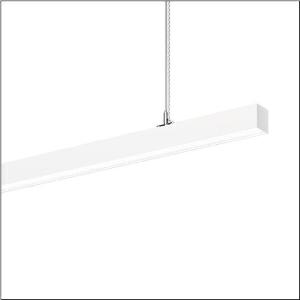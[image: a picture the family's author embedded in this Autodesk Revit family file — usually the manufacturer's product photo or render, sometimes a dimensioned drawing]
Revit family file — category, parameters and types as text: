
# Revit family: silica_r__21_51mx33tbt9w_4d61
name_source: partatom
category: Lighting Fixtures
units: mm (PartAtom-declared; Revit-internal decimal feet)

## family parameters
Cut with Voids When Loaded = No
Host = Face
Light Source = No
Part Type = Normal
Room Calculation Point = No
Round Connector Dimension = Use Diameter
Shared = No

## types (1)
- --- (1 x LED, 7170 lm, 67.4 W, 6500K)
    Apparent Load = 67 VA
    CIE Flux Codes = 78 96 99 56 100
    Color Rendering = 80
    Color Temperature = 6500K
    Default Elevation = 1800 mm
    Description = Silica® 21, office luminaire, primary optical cover: prismatic diffuser, of PMMA, CAT 2 (L<= 3000cd/m²), light emission: direct/indirect distribution, primary light characteristic: symmetric, installation type: suspended mounting, LED, rated luminous flux: 7.170lm, luminous efficacy: 101lm/W, light colour: 8tw, colour temperature: 2700..6500K, control gear: ECG DALI, with terminal, 3+2-pole, max. 2.5mm², mains connection: 220..240V, AC, 50/60Hz, rated input power: 70.8W, luminaire housing, of aluminium, traffic white (RAL 9016), length: 1.504mm, width: 53mm, height: 53mm, protection rating (complete): IP20, insulation class (complete): insulation class I (protective earthing), certification: CE, permissible operating ambient temperature: 0..+35°C, standard: EN 50419, packaging unit: 1 piece
    Height = 53 mm
    Lamp = 1 x LED
    Lamp Light Flux = 7170 lm
    Lamp Power = 67.4 W
    Lamp count = 1
    Length = 1504 mm
    Luminous efficacy = 106 lm/W
    Manufacturer = Siteco
    ModVariant = No
    Model = 51MX33TBT9W
    Mounting Place = Ceiling
    Mounting Type = Pendant
    Number of Poles = 1
    OnlyDefault = Yes
    Power Factor = 1
    Product Name = Silica® 21
    Product group = office luminaire | ceiling pendant
    ProductGroupID = 902
    Protection Class = Protection class I
    Protection Degree = IP 20
    RLX_Detail_Level = 1
    RLX_Emergency_Light_Flux = 0 lm
    RLX_Emergency_Type = 0
    RLX_Emergency_Type_DB = No
    RlxData = <blob elided: 18189 chars, md5=375d7aac>
    Socket = socket
    Standby Power = 0 W
    System Light Flux = 7170 lm
    System Power = 67 W
    Type Comments = individual setting
    Type Image = l_1297784.jpg
    URL = http://relux.com
    VarID = @adj_071101
    Voltage = 0 V
    Weight = 0.00 kg
    Width = 53 mm

## geometry (parser evidence)
native form markers: Blend x4, Sweep x13
no freeform markers — native parametric forms only
